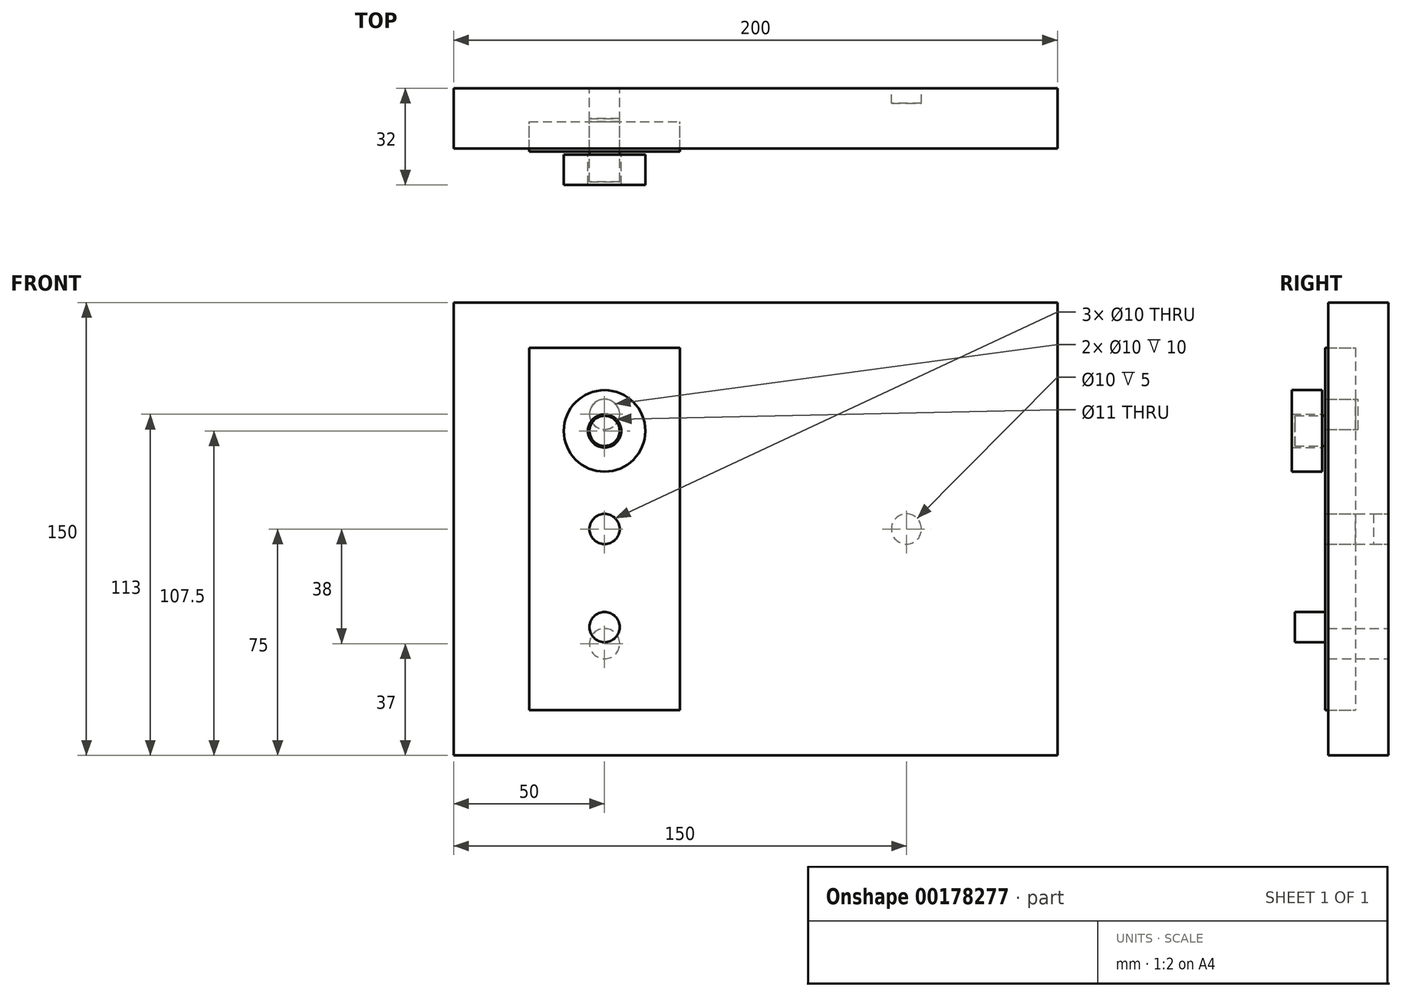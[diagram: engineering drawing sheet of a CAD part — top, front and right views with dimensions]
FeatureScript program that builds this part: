
annotation { "Feature Type Name" : "Feature", "Feature Type Description" : "" }
export const myFeature = defineFeature(function(context is Context, id is Id, definition is map)
    precondition{}
    {
        {
            var Q0;
            Q0=qCreatedBy(makeId("Front.planeOp"),FACE);
            var sketch = newSketch(context, id + "F0", { "sketchPlane" : qUnion([Q0])});
            skLineSegment(sketch, "E0.bottom", {"start": v(100, 75) * mm, "end": v(-100, 75) * mm});
            skLineSegment(sketch, "E0.top", {"start": v(100, -75) * mm, "end": v(-100, -75) * mm});
            skLineSegment(sketch, "E0.left", {"start": v(100, 75) * mm, "end": v(100, -75) * mm});
            skLineSegment(sketch, "E0.right", {"start": v(-100, 75) * mm, "end": v(-100, -75) * mm});
            skPoint(sketch, "E0.middle", {"position": v(0, 0) * mm});
            skLineSegment(sketch, "E1.bottom", {"start": v(100, 19) * mm, "end": v(-100, 19) * mm, "construction": true});
            skLineSegment(sketch, "E1.top", {"start": v(100, -19) * mm, "end": v(-100, -19) * mm, "construction": true});
            skLineSegment(sketch, "E1.left", {"start": v(100, 19) * mm, "end": v(100, -19) * mm, "construction": true});
            skLineSegment(sketch, "E1.right", {"start": v(-100, 14.84) * mm, "end": v(-100, -19) * mm, "construction": true});
            skPoint(sketch, "E2", {"position": v(50, 0) * mm});
            skCircle(sketch, "E3", {"center": v(50, 0) * mm, "radius": 19 * mm, "construction": true});
            skPoint(sketch, "E4", {"position": v(-50, 0) * mm});
            skCircle(sketch, "E5", {"center": v(-50, 38) * mm, "radius": 5 * mm});
            skCircle(sketch, "E6.MirrorC", {"center": v(-50, -38) * mm, "radius": 5 * mm});
            skCircle(sketch, "E7", {"center": v(50, 0) * mm, "radius": 5 * mm});
            skCircle(sketch, "E8.MirrorC", {"center": v(-50, 0) * mm, "radius": 5 * mm});
            skSolve(sketch);
        }
        {
            var Q0;
            Q0=makeQuery(id+"F0.imprint","IMPRINT",FACE,{"disambiguationData":[TD([[makeQuery(id+"F0.imprint","IMPRINT",EDGE,{"derivedFrom":sQuery(id+"F0.wireOp",EDGE,"E0.bottom")}),1.0]])]});
            var Q1;
            Q1=makeQuery(id+"F0.imprint","IMPRINT",FACE,{"disambiguationData":[TD([[makeQuery(id+"F0.imprint","IMPRINT",EDGE,{"derivedFrom":sQuery(id+"F0.wireOp",EDGE,"E5")}),1.0]])]});
            var Q2;
            Q2=makeQuery(id+"F0.imprint","IMPRINT",FACE,{"disambiguationData":[TD([[makeQuery(id+"F0.imprint","IMPRINT",EDGE,{"derivedFrom":sQuery(id+"F0.wireOp",EDGE,"E6.MirrorC")}),-1.0]])]});
            extrude(context, id + "F1", {"entities" : qUnion([Q0, Q1, Q2]), "depth" : 10 * mm});
        }
        {
            var Q0;
            Q0=makeQuery(id+"F0.imprint","IMPRINT",FACE,{"disambiguationData":[TD([[makeQuery(id+"F0.imprint","IMPRINT",EDGE,{"derivedFrom":sQuery(id+"F0.wireOp",EDGE,"E8.MirrorC")}),-1.0]])]});
            var Q1;
            Q1=makeQuery(id+"F0.imprint","IMPRINT",FACE,{"disambiguationData":[TD([[makeQuery(id+"F0.imprint","IMPRINT",EDGE,{"derivedFrom":sQuery(id+"F0.wireOp",EDGE,"E7")}),1.0]])]});
            extrude(context, id + "F2", {"entities" : qUnion([Q0, Q1]), "operationType" : NewBodyOperationType.ADD, "depth" : 20 * mm});
        }
        {
            var Q0;
            {var subQ0=sQuery(id+"F0.wireOp",EDGE,"E8.MirrorC");Q0=makeQuery(id+"FzNsiysy4ztsOz8_2.boolean.opBoolean","MERGE",FACE,{"derivedFrom":[makeQuery(id+"F2.opExtrude","CAP_FACE",FACE,{"disambiguationData":[OSD([subQ0])],"isStart":false}),makeQuery(id+"FzNsiysy4ztsOz8_2.opExtrude","CAP_FACE",FACE,{"disambiguationData":[OSD([subQ0,sQuery(id+"FyUuvjiDZBKfdtO_2.wireOp",EDGE,"aoUqkZuc-UMUI-3g7E-gpQo-OfSRTUkAMcKX.bottom"),sQuery(id+"FyUuvjiDZBKfdtO_2.wireOp",EDGE,"aoUqkZuc-UMUI-3g7E-gpQo-OfSRTUkAMcKX.top"),sQuery(id+"FyUuvjiDZBKfdtO_2.wireOp",EDGE,"aoUqkZuc-UMUI-3g7E-gpQo-OfSRTUkAMcKX.left"),sQuery(id+"FyUuvjiDZBKfdtO_2.wireOp",EDGE,"aoUqkZuc-UMUI-3g7E-gpQo-OfSRTUkAMcKX.right")])],"isStart":false})]});}
            var sketch = newSketch(context, id + "F3", { "sketchPlane" : qUnion([Q0])});
            skPoint(sketch, "E9", {"position": v(-50, 0) * mm});
            skCircle(sketch, "E10", {"center": v(-50, 38) * mm, "radius": 5 * mm});
            skCircle(sketch, "E11.MirrorC", {"center": v(-50, -38) * mm, "radius": 5 * mm});
            skSolve(sketch);
        }
        {
            var Q0;
            Q0=makeQuery(id+"F1.opExtrude","CAP_FACE",FACE,{"disambiguationData":[OSD([sQuery(id+"F0.wireOp",EDGE,"E0.bottom"),sQuery(id+"F0.wireOp",EDGE,"E0.top"),sQuery(id+"F0.wireOp",EDGE,"E0.left"),sQuery(id+"F0.wireOp",EDGE,"E0.right"),sQuery(id+"F0.wireOp",EDGE,"E7"),sQuery(id+"F0.wireOp",EDGE,"E8.MirrorC")])],"isStart":false});
            cPlane(context, id + "F4", {"entities" : qUnion([Q0]), "cplaneType" : CPlaneType.OFFSET, "offset" : 1 * mm, "width" : 150 * mm, "height" : 150 * mm});
        }
        {
            var Q0;
            Q0=qCreatedBy(id+"F4.planeOp",FACE);
            var sketch = newSketch(context, id + "F5", { "sketchPlane" : qUnion([Q0])});
            skLineSegment(sketch, "E12.bottom", {"start": v(-75, 60) * mm, "end": v(-25, 60) * mm});
            skLineSegment(sketch, "E12.top", {"start": v(-75, -60) * mm, "end": v(-25, -60) * mm});
            skLineSegment(sketch, "E12.left", {"start": v(-75, 60) * mm, "end": v(-75, -60) * mm});
            skLineSegment(sketch, "E12.right", {"start": v(-25, 60) * mm, "end": v(-25, -60) * mm});
            skPoint(sketch, "E12.middle", {"position": v(-50, 0) * mm});
            skCircle(sketch, "E13", {"center": v(-50, 0) * mm, "radius": 5 * mm});
            skCircle(sketch, "E14", {"center": v(-50, -38) * mm, "radius": 5 * mm});
            skCircle(sketch, "E15.MirrorC", {"center": v(-50, 38) * mm, "radius": 5 * mm});
            skSolve(sketch);
        }
        {
            var Q0;
            Q0=makeQuery(id+"F5.imprint","IMPRINT",FACE,{"disambiguationData":[TD([[makeQuery(id+"F5.imprint","IMPRINT",EDGE,{"derivedFrom":sQuery(id+"F5.wireOp",EDGE,"E15.MirrorC")}),-1.0]])]});
            var Q1;
            Q1=makeQuery(id+"F5.imprint","IMPRINT",FACE,{"disambiguationData":[TD([[makeQuery(id+"F5.imprint","IMPRINT",EDGE,{"derivedFrom":sQuery(id+"F5.wireOp",EDGE,"E14")}),1.0]])]});
            var Q2;
            Q2=makeQuery(id+"F5.imprint","IMPRINT",FACE,{"disambiguationData":[TD([[makeQuery(id+"F5.imprint","IMPRINT",EDGE,{"derivedFrom":sQuery(id+"F5.wireOp",EDGE,"E12.bottom")}),-1.0]])]});
            extrude(context, id + "F6", {"entities" : qUnion([Q0, Q1, Q2]), "depth" : 10 * mm});
        }
        {
            var Q0;
            Q0=makeQuery(id+"F6.opExtrude","CAP_FACE",FACE,{"disambiguationData":[OSD([sQuery(id+"F5.wireOp",EDGE,"E12.bottom"),sQuery(id+"F5.wireOp",EDGE,"E12.top"),sQuery(id+"F5.wireOp",EDGE,"E12.left"),sQuery(id+"F5.wireOp",EDGE,"E12.right"),sQuery(id+"F5.wireOp",EDGE,"E13"),sQuery(id+"F5.wireOp",EDGE,"E14"),sQuery(id+"F5.wireOp",EDGE,"E15.MirrorC")])],"isStart":false});
            cPlane(context, id + "F7", {"entities" : qUnion([Q0]), "cplaneType" : CPlaneType.OFFSET, "offset" : 1 * mm, "width" : 150 * mm, "height" : 150 * mm});
        }
        {
            var Q0;
            Q0=qCreatedBy(id+"F7.planeOp",FACE);
            var sketch = newSketch(context, id + "F8", { "sketchPlane" : qUnion([Q0])});
            skCircle(sketch, "E16", {"center": v(-50, 32.5) * mm, "radius": 5.5 * mm});
            skCircle(sketch, "E17.0", {"center": v(-50, 32.5) * mm, "radius": 13.5 * mm});
            skSolve(sketch);
        }
        {
            var Q0;
            {var subQ0=sQuery(id+"F0.wireOp",EDGE,"E8.MirrorC");var subQ1=sQuery(id+"F0.wireOp",EDGE,"E7");Q0=makeQuery(id+"F2.boolean.opBoolean","MERGE",FACE,{"derivedFrom":[makeQuery(id+"F1.opExtrude","CAP_FACE",FACE,{"disambiguationData":[OSD([sQuery(id+"F0.wireOp",EDGE,"E0.bottom"),sQuery(id+"F0.wireOp",EDGE,"E0.top"),sQuery(id+"F0.wireOp",EDGE,"E0.left"),sQuery(id+"F0.wireOp",EDGE,"E0.right"),subQ1,subQ0])],"isStart":true}),makeQuery(id+"F2.opExtrude","CAP_FACE",FACE,{"disambiguationData":[OSD([subQ1])],"isStart":true}),makeQuery(id+"F2.opExtrude","CAP_FACE",FACE,{"disambiguationData":[OSD([subQ0])],"isStart":true})]});}
            var sketch = newSketch(context, id + "F9", { "sketchPlane" : qUnion([Q0])});
            skCircle(sketch, "E18", {"center": v(-50, 0) * mm, "radius": 5 * mm});
            skPoint(sketch, "E18.centerSnap0", {"position": v(-100, 0) * mm});
            skSolve(sketch);
        }
        {
            var Q0;
            Q0=qSketchRegion(id+"F9",true);
            extrude(context, id + "F10", {"entities" : qUnion([Q0]), "operationType" : NewBodyOperationType.REMOVE, "oppositeDirection" : true, "depth" : 5 * mm});
        }
        {
            var Q0;
            Q0=qSketchRegion(id+"F8",true);
            extrude(context, id + "F11", {"entities" : qUnion([Q0]), "depth" : 10 * mm});
        }
        {
            var Q0;
            Q0=makeQuery(id+"F6.opExtrude","CAP_FACE",FACE,{"disambiguationData":[OSD([sQuery(id+"F5.wireOp",EDGE,"E12.bottom"),sQuery(id+"F5.wireOp",EDGE,"E12.top"),sQuery(id+"F5.wireOp",EDGE,"E12.left"),sQuery(id+"F5.wireOp",EDGE,"E12.right"),sQuery(id+"F5.wireOp",EDGE,"E13")])],"isStart":false});
            var sketch = newSketch(context, id + "F12", { "sketchPlane" : qUnion([Q0])});
            skCircle(sketch, "E19", {"center": v(-50, 32.5) * mm, "radius": 5 * mm});
            skCircle(sketch, "E20.MirrorC", {"center": v(-50, -32.5) * mm, "radius": 5 * mm});
            skSolve(sketch);
        }
        {
            var Q0;
            Q0=qSketchRegion(id+"F12",true);
            extrude(context, id + "F13", {"entities" : qUnion([Q0]), "operationType" : NewBodyOperationType.ADD, "depth" : 10 * mm});
        }
    });
